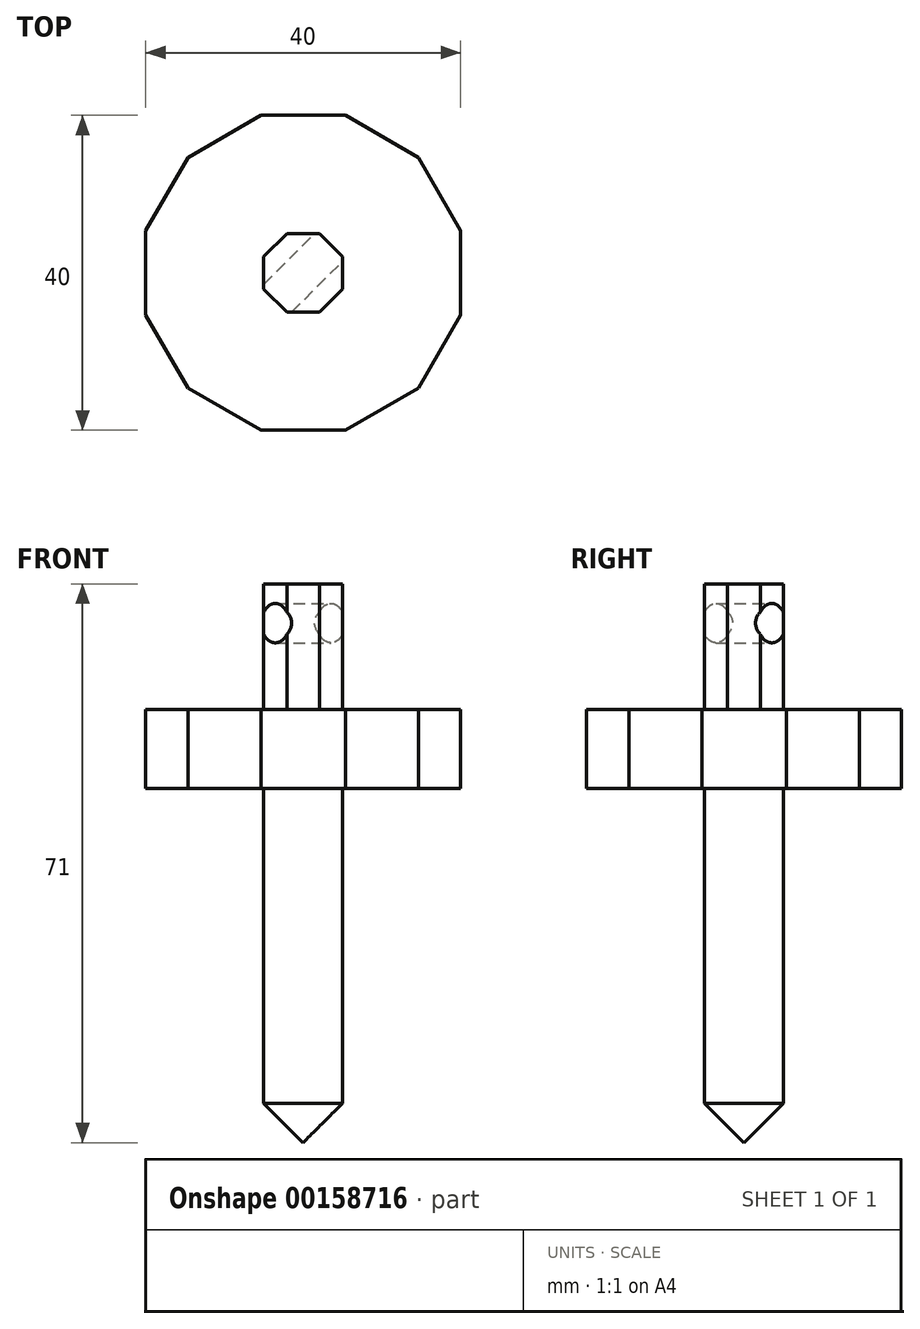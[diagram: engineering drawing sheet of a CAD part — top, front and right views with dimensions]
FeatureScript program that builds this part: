
annotation { "Feature Type Name" : "Feature", "Feature Type Description" : "" }
export const myFeature = defineFeature(function(context is Context, id is Id, definition is map)
    precondition{}
    {
        {
            var Q0;
            Q0=qCreatedBy(makeId("Top.planeOp"),FACE);
            var sketch = newSketch(context, id + "F0", { "sketchPlane" : qUnion([Q0])});
            skCircle(sketch, "E0", {"center": v(0, 0) * mm, "radius": 5 * mm});
            skSolve(sketch);
        }
        {
            var Q0;
            Q0 = qSketchRegion(id + "F0", true);
            extrude(context, id + "F1", {"entities" : qUnion([Q0]), "depth" : 50 * mm});
        }
        {
            var Q0;
            Q0=makeQuery(id+"F1.opExtrude","CAP_EDGE",EDGE,{"disambiguationData":[OSD([sQuery(id+"F0.wireOp",EDGE,"E0")])],"isStart":true});
            chamfer(context, id + "F2", {"entities" : qUnion([Q0]), "width" : 5 * mm, "tangentPropagation" : true});
        }
        {
            var Q0;
            Q0=makeQuery(id+"F1.opExtrude","CAP_FACE",FACE,{"disambiguationData":[OSD([sQuery(id+"F0.wireOp",EDGE,"E0")])],"isStart":false});
            var sketch = newSketch(context, id + "F3", { "sketchPlane" : qUnion([Q0])});
            skCircle(sketch, "E1.cCircle", {"center": v(0, 0) * mm, "radius": 20 * mm, "construction": true});
            skLineSegment(sketch, "E1.0", {"start": v(5.36, -20) * mm, "end": v(-5.36, -20) * mm});
            skLineSegment(sketch, "E1.1", {"start": v(-5.36, -20) * mm, "end": v(-14.64, -14.64) * mm});
            skLineSegment(sketch, "E1.2", {"start": v(-14.64, -14.64) * mm, "end": v(-20, -5.36) * mm});
            skLineSegment(sketch, "E1.3", {"start": v(-20, -5.36) * mm, "end": v(-20, 5.36) * mm});
            skLineSegment(sketch, "E1.4", {"start": v(-20, 5.36) * mm, "end": v(-14.64, 14.64) * mm});
            skLineSegment(sketch, "E1.5", {"start": v(-14.64, 14.64) * mm, "end": v(-5.36, 20) * mm});
            skLineSegment(sketch, "E1.6", {"start": v(-5.36, 20) * mm, "end": v(5.36, 20) * mm});
            skLineSegment(sketch, "E1.7", {"start": v(5.36, 20) * mm, "end": v(14.64, 14.64) * mm});
            skLineSegment(sketch, "E1.8", {"start": v(14.64, 14.64) * mm, "end": v(20, 5.36) * mm});
            skLineSegment(sketch, "E1.9", {"start": v(20, 5.36) * mm, "end": v(20, -5.36) * mm});
            skLineSegment(sketch, "E1.10", {"start": v(20, -5.36) * mm, "end": v(14.64, -14.64) * mm});
            skLineSegment(sketch, "E1.11", {"start": v(14.64, -14.64) * mm, "end": v(5.36, -20) * mm});
            skPoint(sketch, "E1.0.midPoint", {"position": v(0, -20) * mm});
            skLineSegment(sketch, "E2", {"start": v(0, 0) * mm, "end": v(0, -20) * mm});
            skSolve(sketch);
        }
        {
            var Q0;
            {var subQ3=sQuery(id+"F3.wireOp",EDGE,"E1.1");Q0=makeQuery(id+"F3.imprint","IMPRINT",FACE,{"disambiguationData":[TD([[makeQuery(id+"F3.imprint","IMPRINT",EDGE,{"derivedFrom":subQ3}),-1.0]])]});}
            var sketch = newSketch(context, id + "F4", { "sketchPlane" : qUnion([Q0])});
            skSolve(sketch);
        }
        {
            var Q0;
            {var subQ3=sQuery(id+"F3.wireOp",EDGE,"E1.1");Q0=makeQuery(id+"F3.imprint","IMPRINT",FACE,{"disambiguationData":[TD([[makeQuery(id+"F3.imprint","IMPRINT",EDGE,{"derivedFrom":subQ3}),-1.0]])]});}
            extrude(context, id + "F5", {"entities" : qUnion([Q0]), "operationType" : NewBodyOperationType.ADD, "depth" : 5 * mm, "hasSecondDirection" : true, "secondDirectionOppositeDirection" : true, "secondDirectionDepth" : 5 * mm});
        }
        {
            var Q0;
            Q0=makeQuery(id+"F4.imprint","IMPRINT",FACE,{"disambiguationData":[TD([[makeQuery(id+"F4.imprint","IMPRINT",EDGE,{"derivedFrom":makeQuery(id+"F3.imprint","IMPRINT",EDGE,{"derivedFrom":makeQuery(id+"F1.opExtrude","CAP_EDGE",EDGE,{"disambiguationData":[OSD([sQuery(id+"F0.wireOp",EDGE,"E0")])],"isStart":false})})}),1.0]])]});
            extrude(context, id + "F6", {"entities" : qUnion([Q0]), "operationType" : NewBodyOperationType.ADD, "depth" : 5 * mm});
        }
        {
            var Q0;
            {var subQ0=sQuery(id+"F0.wireOp",EDGE,"E0");Q0=makeQuery(id+"F6.boolean.opBoolean","MERGE",FACE,{"derivedFrom":[makeQuery(id+"F5.opExtrude","CAP_FACE",FACE,{"disambiguationData":[OSD([subQ0,sQuery(id+"F3.wireOp",EDGE,"E1.0"),sQuery(id+"F3.wireOp",EDGE,"E1.1"),sQuery(id+"F3.wireOp",EDGE,"E1.2"),sQuery(id+"F3.wireOp",EDGE,"E1.3"),sQuery(id+"F3.wireOp",EDGE,"E1.4"),sQuery(id+"F3.wireOp",EDGE,"E1.5"),sQuery(id+"F3.wireOp",EDGE,"E1.6"),sQuery(id+"F3.wireOp",EDGE,"E1.7"),sQuery(id+"F3.wireOp",EDGE,"E1.8"),sQuery(id+"F3.wireOp",EDGE,"E1.9"),sQuery(id+"F3.wireOp",EDGE,"E1.10"),sQuery(id+"F3.wireOp",EDGE,"E1.11")])],"isStart":false}),makeQuery(id+"F6.opExtrude","CAP_FACE",FACE,{"disambiguationData":[OSD([subQ0])],"isStart":false})]});}
            var sketch = newSketch(context, id + "F7", { "sketchPlane" : qUnion([Q0])});
            skCircle(sketch, "E3.cCircle", {"center": v(0, 0) * mm, "radius": 5 * mm, "construction": true});
            skLineSegment(sketch, "E3.0", {"start": v(-2.07, 5) * mm, "end": v(2.07, 5) * mm});
            skLineSegment(sketch, "E3.1", {"start": v(2.07, 5) * mm, "end": v(5, 2.07) * mm});
            skLineSegment(sketch, "E3.2", {"start": v(5, 2.07) * mm, "end": v(5, -2.07) * mm});
            skLineSegment(sketch, "E3.3", {"start": v(5, -2.07) * mm, "end": v(2.07, -5) * mm});
            skLineSegment(sketch, "E3.4", {"start": v(2.07, -5) * mm, "end": v(-2.07, -5) * mm});
            skLineSegment(sketch, "E3.5", {"start": v(-2.07, -5) * mm, "end": v(-5, -2.07) * mm});
            skLineSegment(sketch, "E3.6", {"start": v(-5, -2.07) * mm, "end": v(-5, 2.07) * mm});
            skLineSegment(sketch, "E3.7", {"start": v(-5, 2.07) * mm, "end": v(-2.07, 5) * mm});
            skPoint(sketch, "E3.0.midPoint", {"position": v(0, 5) * mm});
            skLineSegment(sketch, "E4", {"start": v(0, 0) * mm, "end": v(0, 5) * mm});
            skSolve(sketch);
        }
        {
            var Q0;
            Q0 = qSketchRegion(id + "F7", true);
            extrude(context, id + "F8", {"entities" : qUnion([Q0]), "operationType" : NewBodyOperationType.ADD, "depth" : 16 * mm});
        }
        {
            var Q0;
            Q0=makeQuery(id+"F8.opExtrude","SWEPT_FACE",FACE,{"disambiguationData":[OSD([sQuery(id+"F7.wireOp",EDGE,"E3.1")])]});
            var sketch = newSketch(context, id + "F9", { "sketchPlane" : qUnion([Q0])});
            skLineSegment(sketch, "E5", {"start": v(0, 71) * mm, "end": v(0, 66) * mm});
            skPoint(sketch, "E5.endSnap0", {"position": v(0, 71) * mm});
            skCircle(sketch, "E6", {"center": v(0, 66) * mm, "radius": 2.5 * mm});
            skSolve(sketch);
        }
        {
            var Q0;
            Q0 = qSketchRegion(id + "F9", true);
            extrude(context, id + "F10", {"entities" : qUnion([Q0]), "operationType" : NewBodyOperationType.REMOVE, "oppositeDirection" : true, "depth" : 25 * mm});
        }
    });
